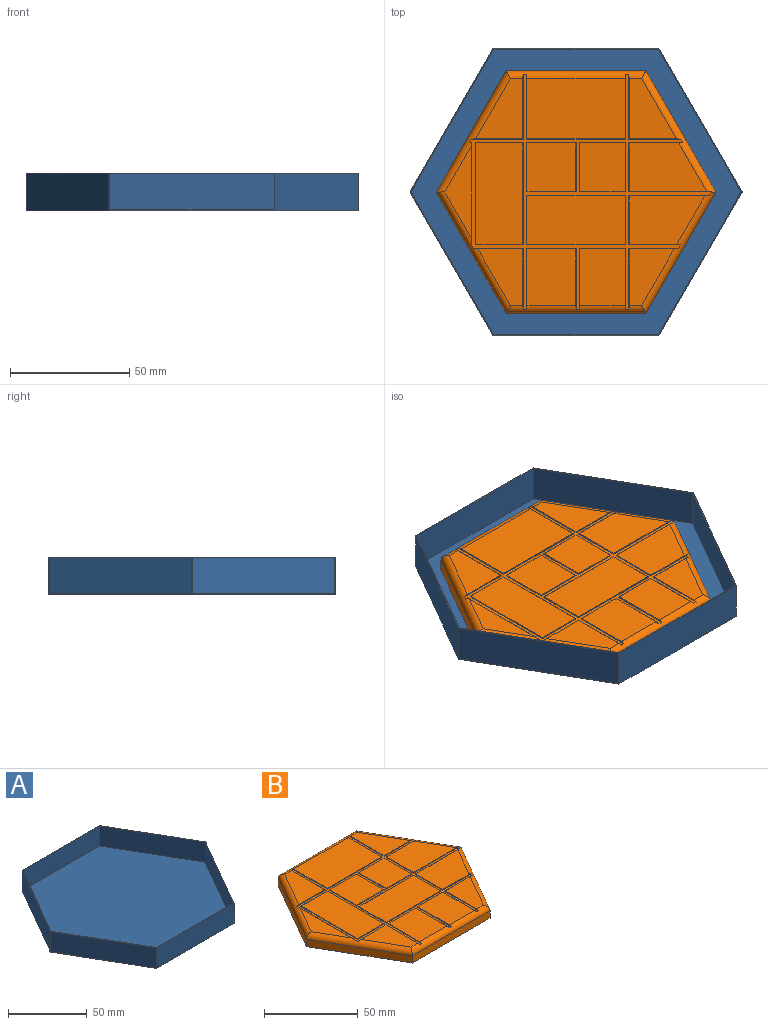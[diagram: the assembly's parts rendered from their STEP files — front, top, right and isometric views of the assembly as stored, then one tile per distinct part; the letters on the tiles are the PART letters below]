
ASSEMBLY  parts=2 mates=1
PART A: 15 faces, bbox 139.3x120.7x15.9 mm
  f0: plane 139.31x120.65mm, normal (0,0,1), area 166.6mm2, adj f1,f2,f3,f4,f5,f6,f8,f9
  f1: plane 60.33x34.83mm, normal (0.87,0.5,0), area 1105.8mm2, adj f0,f2,f6,f7
  f2: plane 69.66x15.88mm, normal (0,1,0), area 1105.8mm2, adj f0,f1,f3,f7
  f3: plane 60.33x34.83mm, normal (-0.87,0.5,0), area 1105.8mm2, adj f0,f2,f4,f7
  f4: plane 60.33x34.83mm, normal (-0.87,-0.5,0), area 1105.8mm2, adj f0,f3,f5,f7
  f5: plane 69.66x15.88mm, normal (0,-1,0), area 1105.8mm2, adj f0,f4,f6,f7
  f6: plane 60.33x34.83mm, normal (0.87,-0.5,0), area 1105.8mm2, adj f0,f1,f5,f7
  f7: plane 139.31x120.65mm, normal (0,0,-1), area 12606.2mm2, adj f1,f2,f3,f4,f5,f6
  f8: plane 59.93x34.6mm, normal (-0.87,-0.5,0), area 1070.8mm2, adj f0,f9,f13,f14
  f9: plane 69.2x15.48mm, normal (0,-1,0), area 1070.8mm2, adj f0,f8,f10,f14
  f10: plane 59.93x34.6mm, normal (0.87,-0.5,0), area 1070.8mm2, adj f0,f9,f11,f14
  f11: plane 59.93x34.6mm, normal (0.87,0.5,0), area 1070.8mm2, adj f0,f10,f12,f14
  f12: plane 69.2x15.48mm, normal (0,1,0), area 1070.8mm2, adj f0,f11,f13,f14
  f13: plane 59.93x34.6mm, normal (-0.87,0.5,0), area 1070.8mm2, adj f0,f8,f12,f14
  f14: plane 138.39x119.85mm, normal (0,0,1), area 12439.6mm2, adj f8,f9,f10,f11,f12,f13
PART B: 110 faces, bbox 117.3x101.6x8 mm
  f0: plane 38.73x11.18mm, normal (0,0,1), area 216.5mm2, adj f12,f13,f95
  f1: plane 25.27x19.74mm, normal (0,0,1), area 314.4mm2, adj f10,f12,f74,f75
  f2: plane 23.75x20.45mm, normal (0,0,1), area 485.6mm2, adj f11,f107,f108,f109
  f3: plane 23.75x18.86mm, normal (0,0,1), area 285mm2, adj f11,f13,f96,f97
  f4: plane 23.75x18.86mm, normal (0,0,1), area 285mm2, adj f11,f22,f98,f99
  f5: plane 31.69x20.45mm, normal (0,0,1), area 527.2mm2, adj f22,f84,f85,f86
  f6: plane 32.57x20.45mm, normal (0,0,1), area 545.2mm2, adj f21,f79,f80,f81
  f7: plane 25.27x19.74mm, normal (0,0,1), area 314.4mm2, adj f10,f21,f82,f83
  f8: plane 23.75x18.92mm, normal (0,0,1), area 449.4mm2, adj f11,f100,f101,f102
  f9: plane 41.15x25.27mm, normal (0,0,1), area 1039.9mm2, adj f10,f76,f77,f78
  f10: cylinder r=3.17mm len=58.66mm, axis (1,0,0), area 280.8mm2, adj f1,f7,f9,f12,f16,f21,f35,f36
  f11: cylinder r=3.17mm len=58.66mm, axis (-1,0,0), area 278.3mm2, adj f2,f3,f4,f8,f13,f19,f22,f42
  f12: cylinder r=3.17mm len=52.39mm, axis (0.5,0.87,0), area 282.6mm2, adj f0,f1,f10,f13,f17,f37,f38,f65
  f13: cylinder r=3.17mm len=52.39mm, axis (-0.5,0.87,0), area 280.9mm2, adj f0,f3,f11,f12,f18,f39,f40,f41
  f14: plane 50.8x29.33mm, normal (0.87,-0.5,0), area 279.4mm2, adj f15,f19,f20,f22
  f15: plane 50.8x29.33mm, normal (0.87,0.5,0), area 279.4mm2, adj f14,f16,f20,f21
  f16: plane 58.66x4.76mm, normal (0,1,0), area 279.4mm2, adj f10,f15,f17,f20
  f17: plane 50.8x29.33mm, normal (-0.87,0.5,0), area 279.4mm2, adj f12,f16,f18,f20
  f18: plane 50.8x29.33mm, normal (-0.87,-0.5,0), area 279.4mm2, adj f13,f17,f19,f20
  f19: plane 58.66x4.76mm, normal (0,-1,0), area 279.4mm2, adj f11,f14,f18,f20
  f20: plane 117.32x101.6mm, normal (0,0,-1), area 8939.6mm2, adj f14,f15,f16,f17,f18,f19
  f21: cylinder r=3.17mm len=52.39mm, axis (0.5,-0.87,0), area 282.9mm2, adj f6,f7,f10,f15,f22,f54,f56,f57
  f22: cylinder r=3.17mm len=52.39mm, axis (-0.5,-0.87,0), area 280.1mm2, adj f4,f5,f11,f14,f21,f50,f51,f53
  f23: plane 19.94x0.25mm, normal (0,1,0), area 5.1mm2, adj f24,f64,f65,f73
  f24: plane 42.93x0.25mm, normal (1,0,0), area 10.9mm2, adj f23,f25,f65,f72
  f25: plane 19.94x0.25mm, normal (0,-1,0), area 5.1mm2, adj f24,f64,f65,f70
  f26: plane 20.7x0.25mm, normal (0,-1,0), area 5.3mm2, adj f27,f60,f65,f91
  f27: plane 20.7x0.25mm, normal (-1,0,0), area 5.3mm2, adj f26,f28,f65,f92
  f28: plane 20.7x0.25mm, normal (0,1,0), area 5.3mm2, adj f27,f60,f65,f94
  f29: plane 41.4x0.25mm, normal (0,1,0), area 10.5mm2, adj f30,f61,f65,f106
  f30: plane 20.7x0.25mm, normal (1,0,0), area 5.3mm2, adj f29,f31,f65,f105
  f31: plane 41.4x0.25mm, normal (0,-1,0), area 10.5mm2, adj f30,f61,f65,f103
  f32: plane 19.18x0.25mm, normal (0,1,0), area 4.9mm2, adj f33,f62,f65,f89
  f33: plane 20.7x0.25mm, normal (1,0,0), area 5.3mm2, adj f32,f34,f65,f87
  f34: plane 19.18x0.25mm, normal (0,-1,0), area 4.9mm2, adj f33,f62,f65,f88
  f35: plane 26.91x0.25mm, normal (-1,0,0), area 6.8mm2, adj f10,f63,f65,f76
  f36: plane 26.91x0.25mm, normal (1,0,0), area 6.8mm2, adj f10,f37,f65,f74
  f37: plane 21.69x0.26mm, normal (0,-1,0), area 5.4mm2, adj f12,f36,f65,f75
  f38: plane 1.11x0.33mm, normal (0,1,0), area 0.2mm2, adj f12,f39,f65,f95
  f39: plane 42.94x0.26mm, normal (1,0,0), area 10.8mm2, adj f13,f38,f40,f65,f95
  f40: plane 0.22x0.09mm, normal (0,-1,0), area 0mm2, adj f13,f39,f65
  f41: plane 20.81x0.26mm, normal (0,1,0), area 5.2mm2, adj f13,f42,f65,f97
  f42: plane 25.38x0.25mm, normal (1,0,0), area 6.4mm2, adj f11,f41,f65,f96
  f43: plane 25.38x0.25mm, normal (-1,0,0), area 6.4mm2, adj f11,f44,f65,f107
  f44: plane 20.7x0.25mm, normal (0,1,0), area 5.3mm2, adj f43,f45,f65,f109
  f45: plane 25.38x0.25mm, normal (1,0,0), area 6.4mm2, adj f11,f44,f65,f108
  f46: plane 25.38x0.25mm, normal (-1,0,0), area 6.4mm2, adj f11,f47,f65,f102
  f47: plane 19.18x0.25mm, normal (0,1,0), area 4.9mm2, adj f46,f48,f65,f101
  f48: plane 25.38x0.25mm, normal (1,0,0), area 6.4mm2, adj f11,f47,f65,f100
  f49: plane 25.38x0.25mm, normal (-1,0,0), area 6.4mm2, adj f11,f50,f65,f98
  f50: plane 20.81x0.26mm, normal (0,1,0), area 5.2mm2, adj f22,f49,f65,f99
  f51: plane 21.69x0.26mm, normal (0,-1,0), area 5.4mm2, adj f22,f52,f65,f84
  f52: plane 20.7x0.25mm, normal (-1,0,0), area 5.3mm2, adj f51,f53,f65,f85
  f53: plane 33.64x0.26mm, normal (0,1,0), area 8.5mm2, adj f22,f52,f65,f86
  f54: plane 34.52x0.26mm, normal (0,-1,0), area 8.7mm2, adj f21,f55,f65,f79
  f55: plane 20.7x0.25mm, normal (-1,0,0), area 5.3mm2, adj f54,f56,f65,f80
  f56: plane 22.56x0.26mm, normal (0,1,0), area 5.6mm2, adj f21,f55,f65,f81
  f57: plane 21.69x0.26mm, normal (0,-1,0), area 5.4mm2, adj f21,f58,f65,f83
  f58: plane 26.91x0.25mm, normal (-1,0,0), area 6.8mm2, adj f10,f57,f65,f82
  f59: plane 26.91x0.25mm, normal (1,0,0), area 6.8mm2, adj f10,f63,f65,f78
  f60: plane 20.7x0.25mm, normal (1,0,0), area 5.3mm2, adj f26,f28,f65,f93
  f61: plane 20.7x0.25mm, normal (-1,0,0), area 5.3mm2, adj f29,f31,f65,f104
  f62: plane 20.7x0.25mm, normal (-1,0,0), area 5.3mm2, adj f32,f34,f65,f90
  f63: plane 41.4x0.25mm, normal (0,-1,0), area 10.5mm2, adj f35,f59,f65,f77
  f64: plane 42.93x0.25mm, normal (-1,0,0), area 10.9mm2, adj f23,f25,f65,f71
  f65: plane 101.52x98.27mm, normal (0,0,1), area 808.5mm2, adj f10,f11,f12,f13,f21,f22,f23,f24
  f66: plane 20.45x18.92mm, normal (0,0,1), area 386.9mm2, adj f87,f88,f89,f90
  f67: plane 41.15x20.45mm, normal (0,0,1), area 841.4mm2, adj f103,f104,f105,f106
  f68: plane 20.45x20.45mm, normal (0,0,1), area 418.1mm2, adj f91,f92,f93,f94
  f69: plane 42.67x19.68mm, normal (0,0,1), area 839.9mm2, adj f70,f71,f72,f73
  f70: plane 19.94x0.13mm, normal (0,-0.71,0.71), area 3.6mm2, adj f25,f69,f71,f72
  f71: plane 42.93x0.13mm, normal (-0.71,0,0.71), area 7.7mm2, adj f64,f69,f70,f73
  f72: plane 42.93x0.13mm, normal (0.71,0,0.71), area 7.7mm2, adj f24,f69,f70,f73
  f73: plane 19.94x0.13mm, normal (0,0.71,0.71), area 3.6mm2, adj f23,f69,f71,f72
  f74: plane 26.29x0.13mm, normal (0.71,0,0.71), area 4.7mm2, adj f1,f10,f36,f75
  f75: plane 20.96x0.13mm, normal (0,-0.71,0.71), area 3.7mm2, adj f1,f12,f37,f74
  f76: plane 26.29x0.13mm, normal (-0.71,0,0.71), area 4.7mm2, adj f9,f10,f35,f77
  f77: plane 41.4x0.13mm, normal (0,-0.71,0.71), area 7.4mm2, adj f9,f63,f76,f78
  f78: plane 26.29x0.13mm, normal (0.71,0,0.71), area 4.7mm2, adj f9,f10,f59,f77
  f79: plane 33.79x0.13mm, normal (0,-0.71,0.71), area 6mm2, adj f6,f21,f54,f80
  f80: plane 20.7x0.13mm, normal (-0.71,0,0.71), area 3.7mm2, adj f6,f55,f79,f81
  f81: plane 21.84x0.13mm, normal (0,0.71,0.71), area 3.9mm2, adj f6,f21,f56,f80
  f82: plane 26.29x0.13mm, normal (-0.71,0,0.71), area 4.7mm2, adj f7,f10,f58,f83
  f83: plane 20.96x0.13mm, normal (0,-0.71,0.71), area 3.7mm2, adj f7,f21,f57,f82
  f84: plane 20.96x0.13mm, normal (0,-0.71,0.71), area 3.7mm2, adj f5,f22,f51,f85
  f85: plane 20.7x0.13mm, normal (-0.71,0,0.71), area 3.7mm2, adj f5,f52,f84,f86
  f86: plane 32.91x0.13mm, normal (0,0.71,0.71), area 5.8mm2, adj f5,f22,f53,f85
  f87: plane 20.7x0.13mm, normal (0.71,0,0.71), area 3.7mm2, adj f33,f66,f88,f89
  f88: plane 19.18x0.13mm, normal (0,-0.71,0.71), area 3.4mm2, adj f34,f66,f87,f90
  f89: plane 19.18x0.13mm, normal (0,0.71,0.71), area 3.4mm2, adj f32,f66,f87,f90
  f90: plane 20.7x0.13mm, normal (-0.71,0,0.71), area 3.7mm2, adj f62,f66,f88,f89
  f91: plane 20.7x0.13mm, normal (0,-0.71,0.71), area 3.7mm2, adj f26,f68,f92,f93
  f92: plane 20.7x0.13mm, normal (-0.71,0,0.71), area 3.7mm2, adj f27,f68,f91,f94
  f93: plane 20.7x0.13mm, normal (0.71,0,0.71), area 3.7mm2, adj f60,f68,f91,f94
  f94: plane 20.7x0.13mm, normal (0,0.71,0.71), area 3.7mm2, adj f28,f68,f92,f93
  f95: plane 42.06x0.13mm, normal (0.71,0,0.71), area 7.4mm2, adj f0,f12,f13,f38,f39
  f96: plane 24.77x0.13mm, normal (0.71,0,0.71), area 4.4mm2, adj f3,f11,f42,f97
  f97: plane 20.08x0.13mm, normal (0,0.71,0.71), area 3.5mm2, adj f3,f13,f41,f96
  f98: plane 24.77x0.13mm, normal (-0.71,0,0.71), area 4.4mm2, adj f4,f11,f49,f99
  f99: plane 20.08x0.13mm, normal (0,0.71,0.71), area 3.5mm2, adj f4,f22,f50,f98
  f100: plane 24.77x0.13mm, normal (0.71,0,0.71), area 4.4mm2, adj f8,f11,f48,f101
  f101: plane 19.18x0.13mm, normal (0,0.71,0.71), area 3.4mm2, adj f8,f47,f100,f102
  f102: plane 24.77x0.13mm, normal (-0.71,0,0.71), area 4.4mm2, adj f8,f11,f46,f101
  f103: plane 41.4x0.13mm, normal (0,-0.71,0.71), area 7.4mm2, adj f31,f67,f104,f105
  f104: plane 20.7x0.13mm, normal (-0.71,0,0.71), area 3.7mm2, adj f61,f67,f103,f106
  f105: plane 20.7x0.13mm, normal (0.71,0,0.71), area 3.7mm2, adj f30,f67,f103,f106
  f106: plane 41.4x0.13mm, normal (0,0.71,0.71), area 7.4mm2, adj f29,f67,f104,f105
  f107: plane 24.77x0.13mm, normal (-0.71,0,0.71), area 4.4mm2, adj f2,f11,f43,f109
  f108: plane 24.77x0.13mm, normal (0.71,0,0.71), area 4.4mm2, adj f2,f11,f45,f109
  f109: plane 20.7x0.13mm, normal (0,0.71,0.71), area 3.7mm2, adj f2,f44,f107,f108
PLACE A at identity fixed
PLACE B t=(0,0,0.4)mm
MATE fastened A.f14 <-> B.f20  axis (0,0,1) through (0,0,0.4)mm
